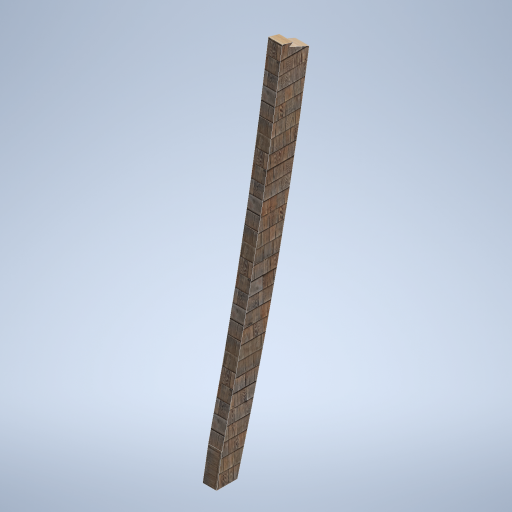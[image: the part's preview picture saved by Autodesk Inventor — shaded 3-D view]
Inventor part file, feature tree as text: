
AUTODESK INVENTOR PART (.ipt)
format: ipt  version: 2024.2 (Build 282272000, 272)  size: 322,560 bytes
history: native  units: in
note: dims shown in document units (in); Inventor stores cm internally (conversion verified against a paired STEP export)
features: other x3, sketch x1
ambient origin geometry x8: Origin, YZ Plane, XZ Plane, XY Plane, X Axis, Y Axis, Z Axis, Center Point
bodies: Solid1 (feature_tree)
feature tree (4):
  other  "side_curve_beam_02.ipt"
  other  "Solid1::side_curve_beam_02.ipt"
  other  "TaggingFeature1"
  sketch  "Sketch1"  dims[d0=0.3937in]
